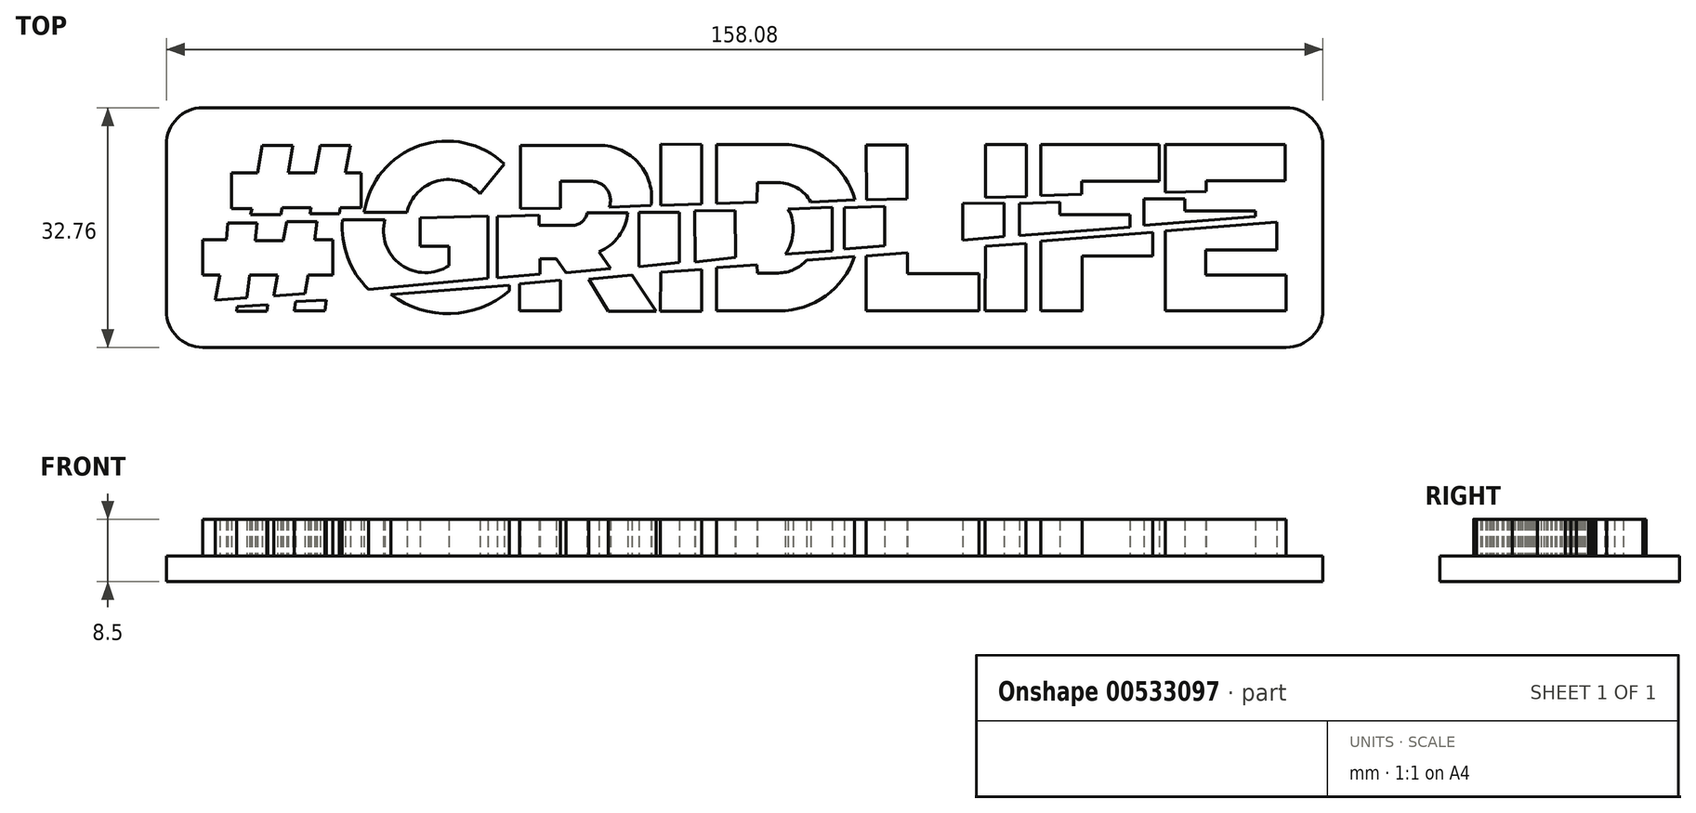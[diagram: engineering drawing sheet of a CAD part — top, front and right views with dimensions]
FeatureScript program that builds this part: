
annotation { "Feature Type Name" : "Feature", "Feature Type Description" : "" }
export const myFeature = defineFeature(function(context is Context, id is Id, definition is map)
    precondition{}
    {
        {
            var Q0;
            Q0=qCreatedBy(makeId("Top.planeOp"),FACE);
            var sketch = newSketch(context, id + "F0", { "sketchPlane" : qUnion([Q0])});
            skLineSegment(sketch, "E0", {"start": v(-70.4, 7.4) * mm, "end": v(-66.84, 7.4) * mm});
            skLineSegment(sketch, "E1", {"start": v(-66.84, 7.4) * mm, "end": v(-66.2, 11.15) * mm});
            skLineSegment(sketch, "E2", {"start": v(-66.2, 11.15) * mm, "end": v(-61.99, 11.15) * mm});
            skLineSegment(sketch, "E3", {"start": v(-61.99, 11.15) * mm, "end": v(-62.63, 7.4) * mm});
            skLineSegment(sketch, "E4", {"start": v(-62.63, 7.4) * mm, "end": v(-58.97, 7.4) * mm});
            skLineSegment(sketch, "E5", {"start": v(-58.97, 7.4) * mm, "end": v(-58.24, 11.15) * mm});
            skLineSegment(sketch, "E6", {"start": v(-58.24, 11.15) * mm, "end": v(-54.12, 11.15) * mm});
            skLineSegment(sketch, "E7", {"start": v(-54.12, 11.15) * mm, "end": v(-54.85, 7.4) * mm});
            skLineSegment(sketch, "E8", {"start": v(-54.85, 7.4) * mm, "end": v(-52.66, 7.4) * mm});
            skLineSegment(sketch, "E9", {"start": v(-52.66, 7.4) * mm, "end": v(-52.66, 2.65) * mm});
            skLineSegment(sketch, "E10", {"start": v(-52.66, 2.65) * mm, "end": v(-55.5, 2.65) * mm});
            skLineSegment(sketch, "E11", {"start": v(-55.5, 2.65) * mm, "end": v(-55.66, 1.84) * mm});
            skLineSegment(sketch, "E12", {"start": v(-55.66, 1.84) * mm, "end": v(-59.68, 1.84) * mm});
            skLineSegment(sketch, "E13", {"start": v(-59.68, 1.84) * mm, "end": v(-59.51, 2.67) * mm});
            skLineSegment(sketch, "E14", {"start": v(-59.51, 2.67) * mm, "end": v(-63.5, 2.67) * mm});
            skLineSegment(sketch, "E15", {"start": v(-63.5, 2.67) * mm, "end": v(-63.68, 1.7) * mm});
            skLineSegment(sketch, "E16", {"start": v(-63.68, 1.7) * mm, "end": v(-67.76, 1.7) * mm});
            skLineSegment(sketch, "E17", {"start": v(-67.76, 1.7) * mm, "end": v(-67.6, 2.53) * mm});
            skLineSegment(sketch, "E18", {"start": v(-67.6, 2.53) * mm, "end": v(-70.28, 2.53) * mm});
            skLineSegment(sketch, "E19", {"start": v(-70.4, 7.4) * mm, "end": v(-70.4, 2.53) * mm});
            skLineSegment(sketch, "E20", {"start": v(-70.4, 2.53) * mm, "end": v(-70.28, 2.53) * mm});
            skLineSegment(sketch, "E21", {"start": v(-70.86, 0.56) * mm, "end": v(-66.88, 0.56) * mm});
            skLineSegment(sketch, "E22", {"start": v(-66.88, 0.56) * mm, "end": v(-67.13, -1.87) * mm});
            skLineSegment(sketch, "E23", {"start": v(-67.13, -1.87) * mm, "end": v(-63.31, -1.87) * mm});
            skLineSegment(sketch, "E24", {"start": v(-63.31, -1.87) * mm, "end": v(-62.8, 0.77) * mm});
            skLineSegment(sketch, "E25", {"start": v(-62.8, 0.77) * mm, "end": v(-58.7, 0.77) * mm});
            skLineSegment(sketch, "E26", {"start": v(-58.7, 0.77) * mm, "end": v(-59.04, -1.7) * mm});
            skLineSegment(sketch, "E27", {"start": v(-59.04, -1.7) * mm, "end": v(-56.52, -1.7) * mm});
            skLineSegment(sketch, "E28", {"start": v(-56.52, -1.7) * mm, "end": v(-56.52, -6.57) * mm});
            skLineSegment(sketch, "E29", {"start": v(-56.52, -6.57) * mm, "end": v(-59.92, -6.57) * mm});
            skLineSegment(sketch, "E30", {"start": v(-59.92, -6.57) * mm, "end": v(-60.34, -9.09) * mm});
            skLineSegment(sketch, "E31", {"start": v(-60.34, -9.09) * mm, "end": v(-64.61, -9.42) * mm});
            skLineSegment(sketch, "E32", {"start": v(-64.61, -9.42) * mm, "end": v(-64.07, -6.57) * mm});
            skLineSegment(sketch, "E33", {"start": v(-64.07, -6.57) * mm, "end": v(-67.93, -6.57) * mm});
            skLineSegment(sketch, "E34", {"start": v(-67.93, -6.57) * mm, "end": v(-68.3, -9.67) * mm});
            skLineSegment(sketch, "E35", {"start": v(-68.3, -9.67) * mm, "end": v(-72.58, -10) * mm});
            skLineSegment(sketch, "E36", {"start": v(-72.58, -10) * mm, "end": v(-72, -6.57) * mm});
            skLineSegment(sketch, "E37", {"start": v(-72, -6.57) * mm, "end": v(-74.3, -6.57) * mm});
            skLineSegment(sketch, "E38", {"start": v(-74.3, -6.57) * mm, "end": v(-74.3, -1.75) * mm});
            skLineSegment(sketch, "E39", {"start": v(-74.3, -1.75) * mm, "end": v(-71.07, -1.75) * mm});
            skLineSegment(sketch, "E40", {"start": v(-71.07, -1.75) * mm, "end": v(-70.86, 0.56) * mm});
            skLineSegment(sketch, "E41", {"start": v(-69.63, -10.86) * mm, "end": v(-69.7, -11.52) * mm});
            skLineSegment(sketch, "E42", {"start": v(-69.7, -11.52) * mm, "end": v(-65.57, -11.52) * mm});
            skLineSegment(sketch, "E43", {"start": v(-65.57, -11.52) * mm, "end": v(-65.45, -10.64) * mm});
            skLineSegment(sketch, "E44", {"start": v(-65.45, -10.64) * mm, "end": v(-69.63, -10.86) * mm});
            skLineSegment(sketch, "E45", {"start": v(-61.64, -10.17) * mm, "end": v(-61.84, -11.44) * mm});
            skLineSegment(sketch, "E46", {"start": v(-61.84, -11.44) * mm, "end": v(-57.62, -11.44) * mm});
            skLineSegment(sketch, "E47", {"start": v(-57.62, -11.44) * mm, "end": v(-57.4, -10) * mm});
            skLineSegment(sketch, "E48", {"start": v(-57.4, -10) * mm, "end": v(-61.64, -10.17) * mm});
            skLineSegment(sketch, "E49", {"start": v(-33.08, 8.63) * mm, "end": v(-36.4, 4.54) * mm});
            skLineSegment(sketch, "E50", {"start": v(-52.27, 2) * mm, "end": v(-46.41, 2) * mm});
            skLineSegment(sketch, "E51", {"start": v(-44.58, 1.3) * mm, "end": v(-35.34, 1.5) * mm});
            skLineSegment(sketch, "E52", {"start": v(-35.34, 1.5) * mm, "end": v(-35.34, -7.02) * mm});
            skLineSegment(sketch, "E53", {"start": v(-44.58, 1.3) * mm, "end": v(-44.58, -2.63) * mm});
            skLineSegment(sketch, "E54", {"start": v(-44.58, -2.63) * mm, "end": v(-40.67, -2.63) * mm});
            skLineSegment(sketch, "E55", {"start": v(-40.67, -2.63) * mm, "end": v(-40.67, -5.27) * mm});
            skLineSegment(sketch, "E56", {"start": v(-55.24, 1.03) * mm, "end": v(-49.42, 1.03) * mm});
            skLineSegment(sketch, "E57", {"start": v(-48.6, -9.2) * mm, "end": v(-32.43, -7.94) * mm});
            skLineSegment(sketch, "E58", {"start": v(-32.43, -7.94) * mm, "end": v(-32.43, -8.7) * mm});
            skLineSegment(sketch, "E59", {"start": v(-34.06, 1.44) * mm, "end": v(-34.06, -6.95) * mm});
            skLineSegment(sketch, "E60", {"start": v(-34.06, 1.44) * mm, "end": v(-28.37, 1.66) * mm});
            skLineSegment(sketch, "E61", {"start": v(-28.37, 1.66) * mm, "end": v(-28.37, 0.21) * mm});
            skLineSegment(sketch, "E62", {"start": v(-28.37, 0.21) * mm, "end": v(-23.83, 0.21) * mm});
            skLineSegment(sketch, "E63", {"start": v(-30.9, 2.5) * mm, "end": v(-25.43, 2.6) * mm});
            skLineSegment(sketch, "E64", {"start": v(-25.43, 2.6) * mm, "end": v(-25.43, 6.26) * mm});
            skLineSegment(sketch, "E65", {"start": v(-25.43, 6.26) * mm, "end": v(-21.2, 6.26) * mm});
            skLineSegment(sketch, "E66", {"start": v(-18.75, 2.74) * mm, "end": v(-13.04, 2.96) * mm});
            skLineSegment(sketch, "E67", {"start": v(-30.9, 2.5) * mm, "end": v(-30.9, 11.18) * mm});
            skLineSegment(sketch, "E68", {"start": v(-30.9, 11.18) * mm, "end": v(-20.1, 11.18) * mm});
            skLineSegment(sketch, "E69", {"start": v(-30.99, -7.77) * mm, "end": v(-25.4, -7.27) * mm});
            skLineSegment(sketch, "E70", {"start": v(-25.4, -7.27) * mm, "end": v(-25.4, -11.46) * mm});
            skLineSegment(sketch, "E71", {"start": v(-25.4, -11.46) * mm, "end": v(-31.01, -11.46) * mm});
            skLineSegment(sketch, "E72", {"start": v(-31.01, -11.46) * mm, "end": v(-30.99, -7.77) * mm});
            skLineSegment(sketch, "E73", {"start": v(-21.58, -7.1) * mm, "end": v(-15.65, -6.56) * mm});
            skLineSegment(sketch, "E74", {"start": v(-15.65, -6.56) * mm, "end": v(-12.33, -11.5) * mm});
            skLineSegment(sketch, "E75", {"start": v(-12.33, -11.5) * mm, "end": v(-18.86, -11.5) * mm});
            skLineSegment(sketch, "E76", {"start": v(-18.86, -11.5) * mm, "end": v(-21.58, -7.1) * mm});
            skLineSegment(sketch, "E77", {"start": v(-14.68, 2) * mm, "end": v(-14.68, -5.43) * mm});
            skLineSegment(sketch, "E78", {"start": v(-14.68, -5.43) * mm, "end": v(-9.18, -4.84) * mm});
            skLineSegment(sketch, "E79", {"start": v(-9.18, -4.84) * mm, "end": v(-9.18, 2.04) * mm});
            skLineSegment(sketch, "E80", {"start": v(-9.18, 2.04) * mm, "end": v(-14.68, 2) * mm});
            skLineSegment(sketch, "E81", {"start": v(-11.68, -6.18) * mm, "end": v(-6.15, -5.76) * mm});
            skLineSegment(sketch, "E82", {"start": v(-11.77, -11.5) * mm, "end": v(-6.1, -11.5) * mm});
            skLineSegment(sketch, "E83", {"start": v(-6.15, -5.76) * mm, "end": v(-6.1, -11.5) * mm});
            skLineSegment(sketch, "E84", {"start": v(-11.68, -6.18) * mm, "end": v(-11.77, -11.5) * mm});
            skLineSegment(sketch, "E85", {"start": v(-18.55, -5.7) * mm, "end": v(-24.66, -6.25) * mm});
            skLineSegment(sketch, "E86", {"start": v(-34.06, -6.95) * mm, "end": v(-28.24, -6.42) * mm});
            skLineSegment(sketch, "E87", {"start": v(-28.24, -6.42) * mm, "end": v(-28.24, -4.31) * mm});
            skLineSegment(sketch, "E88", {"start": v(-28.24, -4.31) * mm, "end": v(-26.02, -4.31) * mm});
            skLineSegment(sketch, "E89", {"start": v(-26.02, -4.31) * mm, "end": v(-24.66, -6.25) * mm});
            skLineSegment(sketch, "E90", {"start": v(-35.34, -7.02) * mm, "end": v(-51.68, -8.52) * mm});
            skLineSegment(sketch, "E91", {"start": v(-18.55, -5.7) * mm, "end": v(-20.17, -3.39) * mm});
            skLineSegment(sketch, "E92", {"start": v(-21.78, 1.95) * mm, "end": v(-16.2, 1.99) * mm});
            skLineSegment(sketch, "E93", {"start": v(-11.7, 11.33) * mm, "end": v(-11.7, 2.95) * mm});
            skLineSegment(sketch, "E94", {"start": v(-11.7, 2.95) * mm, "end": v(-6.1, 3.17) * mm});
            skLineSegment(sketch, "E95", {"start": v(-6.1, 3.17) * mm, "end": v(-6.1, 11.27) * mm});
            skLineSegment(sketch, "E96", {"start": v(-6.1, 11.27) * mm, "end": v(-11.7, 11.33) * mm});
            skLineSegment(sketch, "E97", {"start": v(-7.08, 2.2) * mm, "end": v(-1.54, 2.25) * mm});
            skLineSegment(sketch, "E98", {"start": v(-1.54, 2.25) * mm, "end": v(-1.5, -4.17) * mm});
            skLineSegment(sketch, "E99", {"start": v(-1.5, -4.17) * mm, "end": v(-7.02, -4.76) * mm});
            skLineSegment(sketch, "E100", {"start": v(-7.02, -4.76) * mm, "end": v(-7.08, 2.2) * mm});
            skLineSegment(sketch, "E101", {"start": v(-4.07, -5.55) * mm, "end": v(1.46, -5.13) * mm});
            skLineSegment(sketch, "E102", {"start": v(1.46, -5.13) * mm, "end": v(1.47, -6.3) * mm});
            skLineSegment(sketch, "E103", {"start": v(-4.07, -5.55) * mm, "end": v(-4.07, -11.45) * mm});
            skLineSegment(sketch, "E104", {"start": v(-4.07, -11.45) * mm, "end": v(4.45, -11.45) * mm});
            skLineSegment(sketch, "E105", {"start": v(1.47, -6.3) * mm, "end": v(4.38, -6.27) * mm});
            skLineSegment(sketch, "E106", {"start": v(5.33, -3.7) * mm, "end": v(11.7, -3.27) * mm});
            skLineSegment(sketch, "E107", {"start": v(8.21, -4.52) * mm, "end": v(14.8, -4.03) * mm});
            skLineSegment(sketch, "E108", {"start": v(5.71, 2.5) * mm, "end": v(11.7, 2.72) * mm});
            skLineSegment(sketch, "E109", {"start": v(13.4, 2.66) * mm, "end": v(18.88, 2.87) * mm});
            skLineSegment(sketch, "E110", {"start": v(13.4, -3) * mm, "end": v(18.93, -2.58) * mm});
            skLineSegment(sketch, "E111", {"start": v(18.93, -2.58) * mm, "end": v(18.88, 2.87) * mm});
            skLineSegment(sketch, "E112", {"start": v(13.4, 2.66) * mm, "end": v(13.4, -3) * mm});
            skLineSegment(sketch, "E113", {"start": v(-4.12, 3.2) * mm, "end": v(1.46, 3.42) * mm});
            skLineSegment(sketch, "E114", {"start": v(-4.1, 11.31) * mm, "end": v(-4.12, 3.2) * mm});
            skLineSegment(sketch, "E115", {"start": v(1.49, 6.11) * mm, "end": v(1.46, 3.42) * mm});
            skLineSegment(sketch, "E116", {"start": v(1.49, 6.11) * mm, "end": v(4.34, 6.09) * mm});
            skLineSegment(sketch, "E117", {"start": v(8.8, 3.44) * mm, "end": v(14.84, 3.71) * mm});
            skLineSegment(sketch, "E118", {"start": v(16.41, 3.73) * mm, "end": v(21.92, 3.87) * mm});
            skLineSegment(sketch, "E119", {"start": v(21.92, 3.87) * mm, "end": v(21.92, 11.26) * mm});
            skLineSegment(sketch, "E120", {"start": v(21.92, 11.26) * mm, "end": v(16.37, 11.26) * mm});
            skLineSegment(sketch, "E121", {"start": v(16.37, 11.26) * mm, "end": v(16.41, 3.73) * mm});
            skLineSegment(sketch, "E122", {"start": v(16.33, -3.94) * mm, "end": v(21.99, -3.5) * mm});
            skLineSegment(sketch, "E123", {"start": v(21.99, -3.5) * mm, "end": v(21.99, -6.39) * mm});
            skLineSegment(sketch, "E124", {"start": v(21.99, -6.39) * mm, "end": v(31.78, -6.39) * mm});
            skLineSegment(sketch, "E125", {"start": v(31.78, -6.39) * mm, "end": v(31.78, -11.34) * mm});
            skLineSegment(sketch, "E126", {"start": v(16.51, -11.45) * mm, "end": v(31.78, -11.45) * mm});
            skLineSegment(sketch, "E127", {"start": v(31.78, -11.45) * mm, "end": v(31.78, -11.34) * mm});
            skLineSegment(sketch, "E128", {"start": v(16.33, -3.94) * mm, "end": v(16.33, -11.45) * mm});
            skLineSegment(sketch, "E129", {"start": v(16.33, -11.45) * mm, "end": v(16.51, -11.45) * mm});
            skLineSegment(sketch, "E130", {"start": v(29.58, 3.22) * mm, "end": v(29.58, -1.79) * mm});
            skLineSegment(sketch, "E131", {"start": v(29.58, -1.79) * mm, "end": v(35.24, -1.3) * mm});
            skLineSegment(sketch, "E132", {"start": v(35.24, -1.3) * mm, "end": v(35.24, 3.27) * mm});
            skLineSegment(sketch, "E133", {"start": v(35.24, 3.27) * mm, "end": v(29.58, 3.22) * mm});
            skLineSegment(sketch, "E134", {"start": v(32.68, -2.6) * mm, "end": v(38.18, -2.22) * mm});
            skLineSegment(sketch, "E135", {"start": v(38.18, -2.22) * mm, "end": v(38.18, -11.45) * mm});
            skLineSegment(sketch, "E136", {"start": v(38.18, -11.45) * mm, "end": v(32.64, -11.45) * mm});
            skLineSegment(sketch, "E137", {"start": v(32.64, -11.45) * mm, "end": v(32.68, -2.6) * mm});
            skLineSegment(sketch, "E138", {"start": v(32.68, 11.32) * mm, "end": v(38.26, 11.32) * mm});
            skLineSegment(sketch, "E139", {"start": v(38.26, 11.32) * mm, "end": v(38.26, 4.2) * mm});
            skLineSegment(sketch, "E140", {"start": v(38.26, 4.2) * mm, "end": v(32.68, 4.08) * mm});
            skLineSegment(sketch, "E141", {"start": v(32.68, 4.08) * mm, "end": v(32.68, 11.32) * mm});
            skLineSegment(sketch, "E142", {"start": v(40.26, 4.28) * mm, "end": v(45.82, 4.48) * mm});
            skLineSegment(sketch, "E143", {"start": v(45.82, 4.48) * mm, "end": v(45.82, 6.25) * mm});
            skLineSegment(sketch, "E144", {"start": v(45.82, 6.25) * mm, "end": v(56.4, 6.25) * mm});
            skLineSegment(sketch, "E145", {"start": v(56.4, 6.25) * mm, "end": v(56.4, 11.32) * mm});
            skLineSegment(sketch, "E146", {"start": v(56.4, 11.32) * mm, "end": v(40.25, 11.32) * mm});
            skLineSegment(sketch, "E147", {"start": v(40.25, 11.32) * mm, "end": v(40.26, 4.28) * mm});
            skLineSegment(sketch, "E148", {"start": v(37.32, 3.22) * mm, "end": v(42.85, 3.43) * mm});
            skLineSegment(sketch, "E149", {"start": v(42.85, 3.43) * mm, "end": v(42.85, 1.68) * mm});
            skLineSegment(sketch, "E150", {"start": v(42.85, 1.68) * mm, "end": v(52.45, 1.68) * mm});
            skLineSegment(sketch, "E151", {"start": v(52.45, 1.68) * mm, "end": v(52.45, 0) * mm});
            skLineSegment(sketch, "E152", {"start": v(52.45, 0) * mm, "end": v(37.34, -1.16) * mm});
            skLineSegment(sketch, "E153", {"start": v(37.34, -1.16) * mm, "end": v(37.32, 3.22) * mm});
            skLineSegment(sketch, "E154", {"start": v(40.26, -1.91) * mm, "end": v(40.26, -11.45) * mm});
            skLineSegment(sketch, "E155", {"start": v(40.26, -11.45) * mm, "end": v(45.88, -11.45) * mm});
            skLineSegment(sketch, "E156", {"start": v(45.88, -11.45) * mm, "end": v(45.88, -3.94) * mm});
            skLineSegment(sketch, "E157", {"start": v(45.88, -3.94) * mm, "end": v(55.52, -3.94) * mm});
            skLineSegment(sketch, "E158", {"start": v(55.52, -3.94) * mm, "end": v(55.52, -0.68) * mm});
            skLineSegment(sketch, "E159", {"start": v(55.52, -0.68) * mm, "end": v(40.26, -1.91) * mm});
            skLineSegment(sketch, "E160", {"start": v(57.28, -0.53) * mm, "end": v(57.28, -11.45) * mm});
            skLineSegment(sketch, "E161", {"start": v(57.28, -11.45) * mm, "end": v(73.78, -11.45) * mm});
            skLineSegment(sketch, "E162", {"start": v(73.78, -11.45) * mm, "end": v(73.78, -6.53) * mm});
            skLineSegment(sketch, "E163", {"start": v(73.78, -6.53) * mm, "end": v(62.78, -6.53) * mm});
            skLineSegment(sketch, "E164", {"start": v(62.78, -6.53) * mm, "end": v(62.78, -3.13) * mm});
            skLineSegment(sketch, "E165", {"start": v(62.78, -3.13) * mm, "end": v(72.52, -3.13) * mm});
            skLineSegment(sketch, "E166", {"start": v(72.52, -3.13) * mm, "end": v(72.52, 0.7) * mm});
            skLineSegment(sketch, "E167", {"start": v(72.52, 0.7) * mm, "end": v(57.28, -0.53) * mm});
            skLineSegment(sketch, "E168", {"start": v(54.35, 3.83) * mm, "end": v(54.35, 0.27) * mm});
            skLineSegment(sketch, "E169", {"start": v(54.35, 0.27) * mm, "end": v(69.57, 1.44) * mm});
            skLineSegment(sketch, "E170", {"start": v(69.57, 1.44) * mm, "end": v(69.57, 2.24) * mm});
            skLineSegment(sketch, "E171", {"start": v(69.57, 2.24) * mm, "end": v(59.92, 2.24) * mm});
            skLineSegment(sketch, "E172", {"start": v(59.92, 2.24) * mm, "end": v(59.92, 3.88) * mm});
            skLineSegment(sketch, "E173", {"start": v(59.92, 3.88) * mm, "end": v(54.35, 3.83) * mm});
            skLineSegment(sketch, "E174", {"start": v(57.28, 4.75) * mm, "end": v(62.82, 4.9) * mm});
            skLineSegment(sketch, "E175", {"start": v(62.82, 4.9) * mm, "end": v(62.82, 6.32) * mm});
            skLineSegment(sketch, "E176", {"start": v(62.82, 6.32) * mm, "end": v(73.64, 6.32) * mm});
            skLineSegment(sketch, "E177", {"start": v(73.64, 6.32) * mm, "end": v(73.64, 11.32) * mm});
            skLineSegment(sketch, "E178", {"start": v(73.64, 11.32) * mm, "end": v(57.28, 11.32) * mm});
            skLineSegment(sketch, "E179", {"start": v(57.28, 11.32) * mm, "end": v(57.28, 4.75) * mm});
            skLineSegment(sketch, "E180", {"start": v(-4.1, 11.31) * mm, "end": v(4.93, 11.31) * mm});
            skArc(sketch, "E181", {"start": v(14.84, 3.71) * mm, "mid": v(11.18, 9.2) * mm, "end": v(4.93, 11.31) * mm});
            skArc(sketch, "E182", {"start": v(8.8, 3.44) * mm, "mid": v(6.93, 5.37) * mm, "end": v(4.34, 6.09) * mm});
            skArc(sketch, "E183", {"start": v(5.33, -3.7) * mm, "mid": v(6.38, -0.66) * mm, "end": v(5.71, 2.5) * mm});
            skArc(sketch, "E184", {"start": v(4.45, -11.45) * mm, "mid": v(10.81, -9.4) * mm, "end": v(14.8, -4.03) * mm});
            skArc(sketch, "E185", {"start": v(4.38, -6.27) * mm, "mid": v(6.48, -5.8) * mm, "end": v(8.21, -4.52) * mm});
            skArc(sketch, "E186", {"start": v(-33.08, 8.63) * mm, "mid": v(-44.69, 11.13) * mm, "end": v(-52.27, 2) * mm});
            skArc(sketch, "E187", {"start": v(-49.42, 1.03) * mm, "mid": v(-47.22, -5.14) * mm, "end": v(-40.67, -5.27) * mm});
            skArc(sketch, "E188", {"start": v(-55.24, 1.03) * mm, "mid": v(-54.51, -4.14) * mm, "end": v(-51.68, -8.52) * mm});
            skArc(sketch, "E189", {"start": v(-48.6, -9.2) * mm, "mid": v(-40.43, -11.84) * mm, "end": v(-32.43, -8.7) * mm});
            skArc(sketch, "E190", {"start": v(-13.04, 2.96) * mm, "mid": v(-14.69, 8.69) * mm, "end": v(-20.1, 11.18) * mm});
            skArc(sketch, "E191", {"start": v(-18.75, 2.74) * mm, "mid": v(-19.05, 5.14) * mm, "end": v(-21.2, 6.26) * mm});
            skArc(sketch, "E192", {"start": v(-23.83, 0.21) * mm, "mid": v(-22.49, 0.7) * mm, "end": v(-21.78, 1.95) * mm});
            skArc(sketch, "E193", {"start": v(-20.17, -3.39) * mm, "mid": v(-17.45, -1.24) * mm, "end": v(-16.2, 1.99) * mm});
            skArc(sketch, "E194", {"start": v(-36.4, 4.54) * mm, "mid": v(-42.18, 6.32) * mm, "end": v(-46.41, 2) * mm});
            skLineSegment(sketch, "E195", {"start": v(11.7, 2.72) * mm, "end": v(11.7, -3.05) * mm});
            skLineSegment(sketch, "E196", {"start": v(11.7, -3.05) * mm, "end": v(11.7, -3.27) * mm});
            skSolve(sketch);
        }
        {
            var Q0;
            Q0 = qSketchRegion(id + "F0", true);
            extrude(context, id + "F1", {"entities" : qUnion([Q0]), "depth" : 5 * mm, "offsetDistance" : 25 * mm});
        }
        {
            var Q0;
            Q0=makeQuery(id+"F1.opExtrude","CAP_FACE",FACE,{"disambiguationData":[OSD([sQuery(id+"F0.wireOp",EDGE,"E142"),sQuery(id+"F0.wireOp",EDGE,"E143"),sQuery(id+"F0.wireOp",EDGE,"E144"),sQuery(id+"F0.wireOp",EDGE,"E145"),sQuery(id+"F0.wireOp",EDGE,"E146"),sQuery(id+"F0.wireOp",EDGE,"E147")])],"isStart":true});
            var sketch = newSketch(context, id + "F2", { "sketchPlane" : qUnion([Q0])});
            skLineSegment(sketch, "E197.bottom", {"start": v(-79.3, -16.31) * mm, "end": v(78.78, -16.31) * mm});
            skLineSegment(sketch, "E197.top", {"start": v(-79.3, 16.45) * mm, "end": v(78.78, 16.45) * mm});
            skLineSegment(sketch, "E197.left", {"start": v(-79.3, -16.31) * mm, "end": v(-79.3, 16.45) * mm});
            skLineSegment(sketch, "E197.right", {"start": v(78.78, -16.31) * mm, "end": v(78.78, 16.45) * mm});
            skSolve(sketch);
        }
        {
            var Q0;
            Q0 = qSketchRegion(id + "F2", true);
            extrude(context, id + "F3", {"entities" : qUnion([Q0]), "depth" : 3.5 * mm, "offsetDistance" : 25 * mm});
        }
        {
            var Q0;
            Q0=makeQuery(id+"F3.opExtrude","SWEPT_EDGE",EDGE,{"disambiguationData":[OSD([sQuery(id+"F2.wireOp",EDGE,"E197.bottom"),sQuery(id+"F2.wireOp",EDGE,"E197.left")])]});
            var Q1;
            Q1=makeQuery(id+"F3.opExtrude","SWEPT_EDGE",EDGE,{"disambiguationData":[OSD([sQuery(id+"F2.wireOp",EDGE,"E197.top"),sQuery(id+"F2.wireOp",EDGE,"E197.left")])]});
            var Q2;
            Q2=makeQuery(id+"F3.opExtrude","SWEPT_EDGE",EDGE,{"disambiguationData":[OSD([sQuery(id+"F2.wireOp",EDGE,"E197.bottom"),sQuery(id+"F2.wireOp",EDGE,"E197.right")])]});
            var Q3;
            Q3=makeQuery(id+"F3.opExtrude","SWEPT_EDGE",EDGE,{"disambiguationData":[OSD([sQuery(id+"F2.wireOp",EDGE,"E197.top"),sQuery(id+"F2.wireOp",EDGE,"E197.right")])]});
            fillet(context, id + "F4", {"entities" : qUnion([Q0, Q1, Q2, Q3]), "radius" : 5 * mm, "tangentPropagation" : true, "allowEdgeOverflow" : false});
        }
    });
